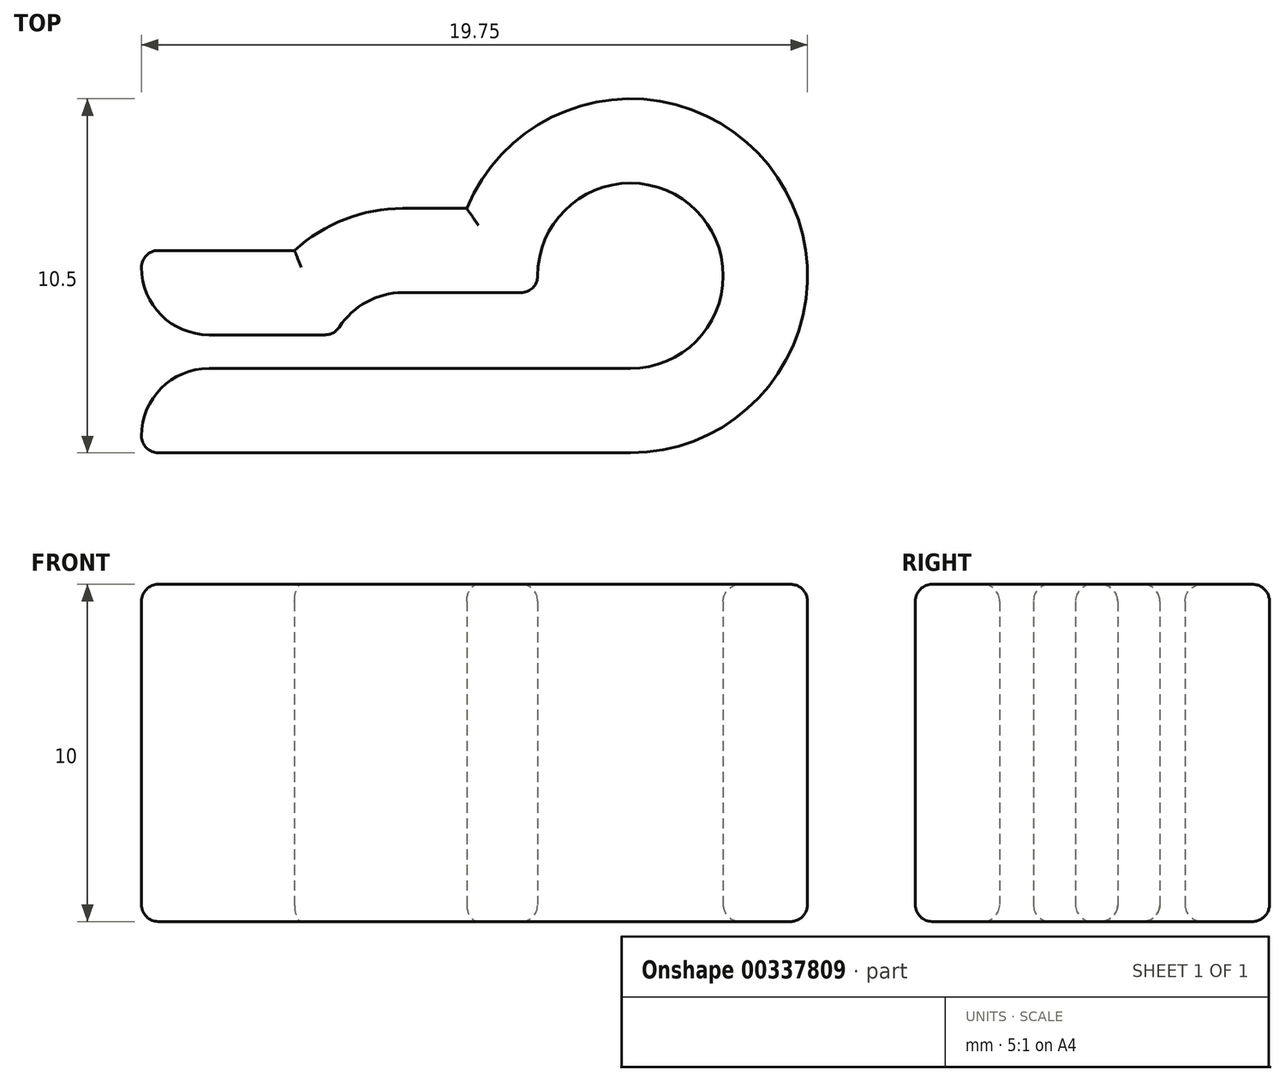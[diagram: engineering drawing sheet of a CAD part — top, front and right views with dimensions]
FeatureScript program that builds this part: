
annotation { "Feature Type Name" : "Feature", "Feature Type Description" : "" }
export const myFeature = defineFeature(function(context is Context, id is Id, definition is map)
    precondition{}
    {
        {
            var Q0;
            Q0=qCreatedBy(makeId("Top.planeOp"),FACE);
            var sketch = newSketch(context, id + "F0", { "sketchPlane" : qUnion([Q0])});
            skCircle(sketch, "E0", {"center": v(0, 0) * mm, "radius": 2.75 * mm});
            skCircle(sketch, "E1", {"center": v(0, 0) * mm, "radius": 5.25 * mm});
            skLineSegment(sketch, "E2.bottom", {"start": v(0, -5.25) * mm, "end": v(-14.5, -5.25) * mm});
            skLineSegment(sketch, "E2.top", {"start": v(0, -2.75) * mm, "end": v(-14.5, -2.75) * mm});
            skLineSegment(sketch, "E2.left", {"start": v(0, -5.25) * mm, "end": v(0, -2.75) * mm});
            skLineSegment(sketch, "E2.right", {"start": v(-14.5, -5.25) * mm, "end": v(-14.5, -2.75) * mm});
            skLineSegment(sketch, "E3", {"start": v(-9.25, 3.82) * mm, "end": v(-9.25, -9.88) * mm, "construction": true});
            skLineSegment(sketch, "E4", {"start": v(-6.75, 3.72) * mm, "end": v(-6.75, -9.58) * mm, "construction": true});
            skLineSegment(sketch, "E5", {"start": v(-11.75, 3.88) * mm, "end": v(-11.75, -9.99) * mm, "construction": true});
            skLineSegment(sketch, "E6.bottom", {"start": v(-14.5, -1.75) * mm, "end": v(0, -1.75) * mm});
            skLineSegment(sketch, "E6.top", {"start": v(-14.5, 0.75) * mm, "end": v(0, 0.75) * mm});
            skLineSegment(sketch, "E6.left", {"start": v(-14.5, -1.75) * mm, "end": v(-14.5, 0.75) * mm});
            skLineSegment(sketch, "E6.right", {"start": v(0, -1.75) * mm, "end": v(0, 0.75) * mm});
            skLineSegment(sketch, "E7", {"start": v(-5.25, -10.29) * mm, "end": v(-5.25, 8.16) * mm, "construction": true});
            skLineSegment(sketch, "E8", {"start": v(-21.12, 0) * mm, "end": v(10.4, 0) * mm, "construction": true});
            skLineSegment(sketch, "E9", {"start": v(-6.75, 2) * mm, "end": v(-4.85, 2) * mm});
            skPoint(sketch, "E10.endSnap0", {"position": v(0, -0.5) * mm});
            skLineSegment(sketch, "E11", {"start": v(-20.05, -0.5) * mm, "end": v(8.9, -0.5) * mm, "construction": true});
            skLineSegment(sketch, "E12", {"start": v(-18.01, 2) * mm, "end": v(8.2, 2) * mm, "construction": true});
            skArc(sketch, "E13", {"start": v(-6.75, 2) * mm, "mid": v(-10.1, 0.6) * mm, "end": v(-11.5, -2.75) * mm});
            skArc(sketch, "E14.trimOffspring", {"start": v(-6.75, -0.5) * mm, "mid": v(-8.34, -1.16) * mm, "end": v(-9, -2.75) * mm});
            skLineSegment(sketch, "E15.bottom", {"start": v(-6.75, -0.5) * mm, "end": v(-1.89, -0.5) * mm});
            skLineSegment(sketch, "E15.top", {"start": v(-6.75, 2) * mm, "end": v(-1.89, 2) * mm});
            skLineSegment(sketch, "E15.left", {"start": v(-6.75, -0.5) * mm, "end": v(-6.75, 2) * mm});
            skLineSegment(sketch, "E16.bottom", {"start": v(-5.25, 0) * mm, "end": v(-2.75, 0) * mm});
            skLineSegment(sketch, "E16.top", {"start": v(-5.25, -1.75) * mm, "end": v(-2.75, -1.75) * mm});
            skLineSegment(sketch, "E16.left", {"start": v(-5.25, 0) * mm, "end": v(-5.25, -1.75) * mm});
            skLineSegment(sketch, "E16.right", {"start": v(-2.75, 0) * mm, "end": v(-2.75, -1.75) * mm});
            skSolve(sketch);
        }
        {
            var Q0;
            {var subQ4=sQuery(id+"F0.wireOp",EDGE,"E2.bottom");Q0=makeQuery(id+"F0.imprint","IMPRINT",FACE,{"disambiguationData":[TD([[makeQuery(id+"F0.imprint","IMPRINT",EDGE,{"derivedFrom":subQ4}),-1.0]])]});}
            var Q1;
            {var subQ0=sQuery(id+"F0.wireOp",EDGE,"E2.left");Q1=makeQuery(id+"F0.imprint","IMPRINT",FACE,{"disambiguationData":[TD([[makeQuery(id+"F0.imprint","IMPRINT",EDGE,{"derivedFrom":subQ0}),1.0]])]});}
            var Q2;
            {var subQ0=sQuery(id+"F0.wireOp",EDGE,"E2.left");Q2=makeQuery(id+"F0.imprint","IMPRINT",FACE,{"disambiguationData":[TD([[makeQuery(id+"F0.imprint","IMPRINT",EDGE,{"derivedFrom":subQ0}),-1.0]])]});}
            var Q3;
            {var subQ0=sQuery(id+"F0.wireOp",EDGE,"E15.top");var subQ1=sQuery(id+"F0.wireOp",EDGE,"E0");var subQ2=makeQuery(id+"F0.imprint","INTERSECT",VERTEX,{"derivedFrom":[subQ1,subQ0]});Q3=makeQuery(id+"F0.imprint","IMPRINT",FACE,{"disambiguationData":[TD([[makeQuery(id+"F0.imprint","IMPRINT",EDGE,{"disambiguationData":[TD([[subQ2,-1.0]])],"derivedFrom":subQ1}),-1.0]])]});}
            var Q4;
            {var subQ0=sQuery(id+"F0.wireOp",EDGE,"E15.top");var subQ1=sQuery(id+"F0.wireOp",EDGE,"E1");var subQ2=makeQuery(id+"F0.imprint","INTERSECT",VERTEX,{"derivedFrom":[subQ1,subQ0]});Q4=makeQuery(id+"F0.imprint","IMPRINT",FACE,{"disambiguationData":[TD([[makeQuery(id+"F0.imprint","IMPRINT",EDGE,{"disambiguationData":[TD([[subQ2,-1.0]])],"derivedFrom":subQ1}),-1.0]])]});}
            var Q5;
            {var subQ0=sQuery(id+"F0.wireOp",EDGE,"E13");var subQ1=sQuery(id+"F0.wireOp",EDGE,"E6.top");var subQ2=makeQuery(id+"F0.imprint","INTERSECT",VERTEX,{"derivedFrom":[subQ1,subQ0]});Q5=makeQuery(id+"F0.imprint","IMPRINT",FACE,{"disambiguationData":[TD([[makeQuery(id+"F0.imprint","IMPRINT",EDGE,{"disambiguationData":[TD([[subQ2,-1.0]])],"derivedFrom":subQ1}),1.0]])]});}
            var Q6;
            {var subQ3=sQuery(id+"F0.wireOp",EDGE,"E6.bottom");var subQ5=sQuery(id+"F0.wireOp",EDGE,"E13");var subQ6=makeQuery(id+"F0.imprint","INTERSECT",VERTEX,{"derivedFrom":[subQ3,subQ5]});Q6=makeQuery(id+"F0.imprint","IMPRINT",FACE,{"disambiguationData":[TD([[makeQuery(id+"F0.imprint","IMPRINT",EDGE,{"disambiguationData":[TD([[subQ6,-1.0]])],"derivedFrom":subQ3}),1.0]])]});}
            var Q7;
            {var subQ0=sQuery(id+"F0.wireOp",EDGE,"E6.left");Q7=makeQuery(id+"F0.imprint","IMPRINT",FACE,{"disambiguationData":[TD([[makeQuery(id+"F0.imprint","IMPRINT",EDGE,{"derivedFrom":subQ0}),-1.0]])]});}
            var Q8;
            {var subQ3=sQuery(id+"F0.wireOp",EDGE,"E6.top");var subQ7=sQuery(id+"F0.wireOp",EDGE,"E1");var subQ9=makeQuery(id+"F0.imprint","INTERSECT",VERTEX,{"derivedFrom":[subQ7,subQ3]});Q8=makeQuery(id+"F0.imprint","IMPRINT",FACE,{"disambiguationData":[TD([[makeQuery(id+"F0.imprint","IMPRINT",EDGE,{"disambiguationData":[TD([[subQ9,1.0]])],"derivedFrom":subQ3}),-1.0]])]});}
            var Q9;
            {var subQ0=sQuery(id+"F0.wireOp",EDGE,"E16.bottom");Q9=makeQuery(id+"F0.imprint","IMPRINT",FACE,{"disambiguationData":[TD([[makeQuery(id+"F0.imprint","IMPRINT",EDGE,{"derivedFrom":subQ0}),-1.0]])]});}
            var Q10;
            {var subQ0=sQuery(id+"F0.wireOp",EDGE,"E16.bottom");Q10=makeQuery(id+"F0.imprint","IMPRINT",FACE,{"disambiguationData":[TD([[makeQuery(id+"F0.imprint","IMPRINT",EDGE,{"derivedFrom":subQ0}),1.0]])]});}
            var Q11;
            {var subQ1=sQuery(id+"F0.wireOp",EDGE,"E1");var subQ3=sQuery(id+"F0.wireOp",EDGE,"E15.bottom");var subQ4=makeQuery(id+"F0.imprint","INTERSECT",VERTEX,{"derivedFrom":[subQ1,subQ3]});Q11=makeQuery(id+"F0.imprint","IMPRINT",FACE,{"disambiguationData":[TD([[makeQuery(id+"F0.imprint","IMPRINT",EDGE,{"disambiguationData":[TD([[subQ4,1.0]])],"derivedFrom":subQ3}),1.0]])]});}
            extrude(context, id + "F1", {"entities" : qUnion([Q0, Q1, Q2, Q3, Q4, Q5, Q6, Q7, Q8, Q9, Q10, Q11]), "endBound" : BoundingType.SYMMETRIC, "depth" : 10 * mm});
        }
        {
            var Q0;
            Q0=makeQuery(id+"F1.opExtrude","CAP_FACE",FACE,{"disambiguationData":[OSD([sQuery(id+"F0.wireOp",EDGE,"E0"),sQuery(id+"F0.wireOp",EDGE,"E1"),sQuery(id+"F0.wireOp",EDGE,"E2.bottom"),sQuery(id+"F0.wireOp",EDGE,"E2.top"),sQuery(id+"F0.wireOp",EDGE,"E2.right"),sQuery(id+"F0.wireOp",EDGE,"E6.bottom"),sQuery(id+"F0.wireOp",EDGE,"E6.top"),sQuery(id+"F0.wireOp",EDGE,"E6.left"),sQuery(id+"F0.wireOp",EDGE,"E13"),sQuery(id+"F0.wireOp",EDGE,"E14.trimOffspring"),sQuery(id+"F0.wireOp",EDGE,"E15.bottom"),sQuery(id+"F0.wireOp",EDGE,"E15.top"),sQuery(id+"F0.wireOp",EDGE,"E16.right")])],"isStart":false});
            var Q1;
            Q1=makeQuery(id+"F1.opExtrude","CAP_FACE",FACE,{"disambiguationData":[OSD([sQuery(id+"F0.wireOp",EDGE,"E0"),sQuery(id+"F0.wireOp",EDGE,"E1"),sQuery(id+"F0.wireOp",EDGE,"E2.bottom"),sQuery(id+"F0.wireOp",EDGE,"E2.top"),sQuery(id+"F0.wireOp",EDGE,"E2.right"),sQuery(id+"F0.wireOp",EDGE,"E6.bottom"),sQuery(id+"F0.wireOp",EDGE,"E6.top"),sQuery(id+"F0.wireOp",EDGE,"E6.left"),sQuery(id+"F0.wireOp",EDGE,"E13"),sQuery(id+"F0.wireOp",EDGE,"E14.trimOffspring"),sQuery(id+"F0.wireOp",EDGE,"E15.bottom"),sQuery(id+"F0.wireOp",EDGE,"E15.top"),sQuery(id+"F0.wireOp",EDGE,"E16.right")])],"isStart":true});
            var Q2;
            Q2=makeQuery(id+"F1.opExtrude","SWEPT_EDGE",EDGE,{"disambiguationData":[OSD([sQuery(id+"F0.wireOp",EDGE,"E6.bottom"),sQuery(id+"F0.wireOp",EDGE,"E14.trimOffspring")])]});
            var Q3;
            Q3=makeQuery(id+"F1.opExtrude","SWEPT_EDGE",EDGE,{"disambiguationData":[OSD([sQuery(id+"F0.wireOp",EDGE,"E15.bottom"),sQuery(id+"F0.wireOp",EDGE,"E16.right")])]});
            var Q4;
            Q4=makeQuery(id+"F1.opExtrude","SWEPT_EDGE",EDGE,{"disambiguationData":[OSD([sQuery(id+"F0.wireOp",EDGE,"E6.top"),sQuery(id+"F0.wireOp",EDGE,"E6.left")])]});
            var Q5;
            Q5=makeQuery(id+"F1.opExtrude","SWEPT_EDGE",EDGE,{"disambiguationData":[OSD([sQuery(id+"F0.wireOp",EDGE,"E2.bottom"),sQuery(id+"F0.wireOp",EDGE,"E2.right")])]});
            fillet(context, id + "F2", {"entities" : qUnion([Q0, Q1, Q2, Q3, Q4, Q5]), "radius" : .5 * mm, "tangentPropagation" : true, "allowEdgeOverflow" : false});
        }
        {
            var Q0;
            Q0=makeQuery(id+"F1.opExtrude","SWEPT_EDGE",EDGE,{"disambiguationData":[OSD([sQuery(id+"F0.wireOp",EDGE,"E6.bottom"),sQuery(id+"F0.wireOp",EDGE,"E6.left")])]});
            var Q1;
            Q1=makeQuery(id+"F1.opExtrude","SWEPT_EDGE",EDGE,{"disambiguationData":[OSD([sQuery(id+"F0.wireOp",EDGE,"E2.top"),sQuery(id+"F0.wireOp",EDGE,"E2.right")])]});
            fillet(context, id + "F3", {"entities" : qUnion([Q0, Q1]), "radius" : 2 * mm, "tangentPropagation" : true, "allowEdgeOverflow" : false});
        }
    });
